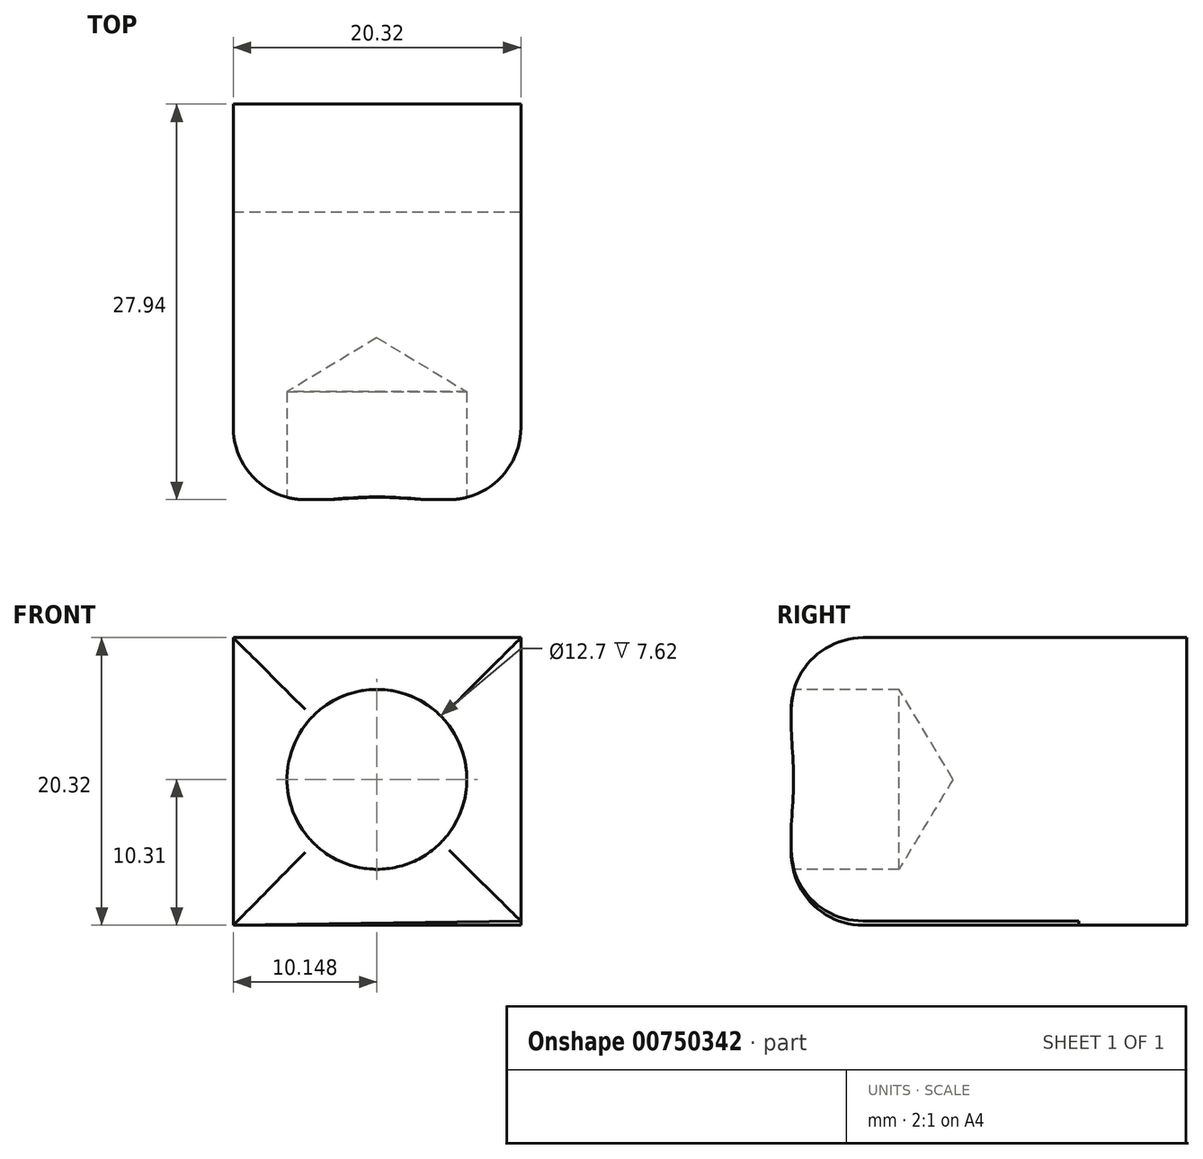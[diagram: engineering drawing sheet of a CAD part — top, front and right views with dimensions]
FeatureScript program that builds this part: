
annotation { "Feature Type Name" : "Feature", "Feature Type Description" : "" }
export const myFeature = defineFeature(function(context is Context, id is Id, definition is map)
    precondition{}
    {
        {
            var Q0;
            Q0=qCreatedBy(makeId("Front.planeOp"),FACE);
            var sketch = newSketch(context, id + "F0", { "sketchPlane" : qUnion([Q0])});
            skLineSegment(sketch, "E0.bottom", {"start": v(-12.3, 10) * mm, "end": v(8.03, 10) * mm});
            skLineSegment(sketch, "E0.top", {"start": v(-12.3, -10.31) * mm, "end": v(8.03, -10.31) * mm});
            skLineSegment(sketch, "E0.left", {"start": v(-12.3, 10) * mm, "end": v(-12.3, -10.31) * mm});
            skLineSegment(sketch, "E0.right", {"start": v(8.03, 10) * mm, "end": v(8.03, -10.31) * mm});
            skSolve(sketch);
        }
        {
            var Q0;
            Q0 = qSketchRegion(id + "F0", true);
            extrude(context, id + "F1", {"entities" : qUnion([Q0]), "depth" : 7.62 * mm, "offsetDistance" : 25.4 * mm});
        }
        {
            var Q0;
            Q0=makeQuery(id+"F1.opExtrude","CAP_FACE",FACE,{"disambiguationData":[OSD([sQuery(id+"F0.wireOp",EDGE,"E0.bottom"),sQuery(id+"F0.wireOp",EDGE,"E0.top"),sQuery(id+"F0.wireOp",EDGE,"E0.left"),sQuery(id+"F0.wireOp",EDGE,"E0.right")])],"isStart":false});
            var sketch = newSketch(context, id + "F2", { "sketchPlane" : qUnion([Q0])});
            skLineSegment(sketch, "E1.bottom", {"start": v(-12.3, -10.31) * mm, "end": v(8.03, -10.01) * mm});
            skLineSegment(sketch, "E1.top", {"start": v(-12.3, 10) * mm, "end": v(8.03, 10) * mm});
            skLineSegment(sketch, "E1.left", {"start": v(-12.3, -10.31) * mm, "end": v(-12.3, 10) * mm});
            skLineSegment(sketch, "E1.right", {"start": v(8.03, -10.01) * mm, "end": v(8.03, 10) * mm});
            skPoint(sketch, "E2", {"position": v(-2.13, 0) * mm});
            skSolve(sketch);
        }
        {
            var Q0;
            Q0 = qSketchRegion(id + "F2", true);
            extrude(context, id + "F3", {"entities" : qUnion([Q0]), "operationType" : NewBodyOperationType.ADD, "depth" : 20.32 * mm, "offsetDistance" : 25.4 * mm});
        }
        {
            var Q0;
            Q0=makeQuery(id+"F3.opExtrude","CAP_FACE",FACE,{"disambiguationData":[OSD([sQuery(id+"F2.wireOp",EDGE,"E1.bottom"),sQuery(id+"F2.wireOp",EDGE,"E1.top"),sQuery(id+"F2.wireOp",EDGE,"E1.left"),sQuery(id+"F2.wireOp",EDGE,"E1.right")])],"isStart":false});
            var sketch = newSketch(context, id + "F4", { "sketchPlane" : qUnion([Q0])});
            skPoint(sketch, "E3", {"position": v(-2.14, 0) * mm});
            skSolve(sketch);
        }
        {
            var Q0;
            Q0=sQuery(id+"F4.wireOp",VERTEX,"E3");
            var Q1;
            Q1=makeQuery(id+"F1.opExtrude","SWEPT_BODY",BODY,{"disambiguationData":[OSD([sQuery(id+"F0.wireOp",EDGE,"E0.bottom"),sQuery(id+"F0.wireOp",EDGE,"E0.top"),sQuery(id+"F0.wireOp",EDGE,"E0.left"),sQuery(id+"F0.wireOp",EDGE,"E0.right")])]});
            hole(context, id + "F5", {"style" : HoleStyle.SIMPLE, "endStyle" : HoleEndStyle.BLIND, "holeDiameter" : 12.7 * mm, "majorDiameter" : 6.35 * mm, "holeDepth" : 7.62 * mm, "isTappedThrough" : true, "tappedDepth" : 12.7 * mm, "tapClearance" : 3, "startFromSketch" : true, "locations" : qUnion([Q0]), "scope" : qUnion([Q1])});
        }
        {
            var Q0;
            Q0=makeQuery(id+"F3.opExtrude","CAP_EDGE",EDGE,{"disambiguationData":[OSD([sQuery(id+"F2.wireOp",EDGE,"E1.top")])],"isStart":false});
            var Q1;
            Q1=makeQuery(id+"F3.opExtrude","CAP_EDGE",EDGE,{"disambiguationData":[OSD([sQuery(id+"F2.wireOp",EDGE,"E1.right")])],"isStart":false});
            var Q2;
            Q2=makeQuery(id+"F3.opExtrude","CAP_EDGE",EDGE,{"disambiguationData":[OSD([sQuery(id+"F2.wireOp",EDGE,"E1.left")])],"isStart":false});
            var Q3;
            Q3=makeQuery(id+"F3.opExtrude","CAP_EDGE",EDGE,{"disambiguationData":[OSD([sQuery(id+"F2.wireOp",EDGE,"E1.bottom")])],"isStart":false});
            fillet(context, id + "F6", {"entities" : qUnion([Q0, Q1, Q2, Q3]), "radius" : 5.08 * mm, "tangentPropagation" : true, "allowEdgeOverflow" : false});
        }
    });
